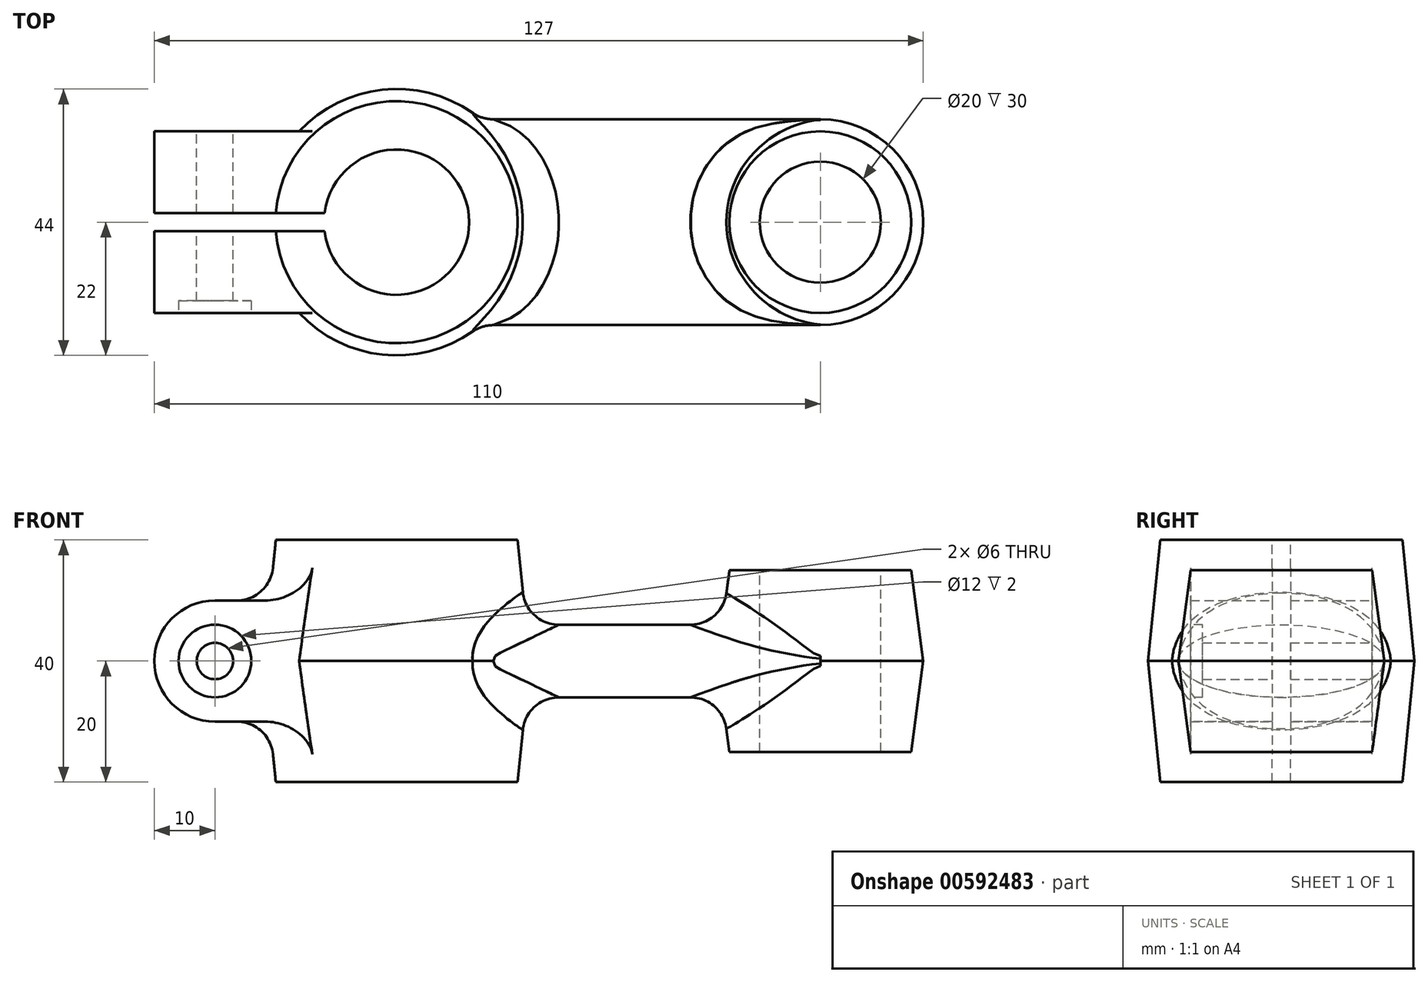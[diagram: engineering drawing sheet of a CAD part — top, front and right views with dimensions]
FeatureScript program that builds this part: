
annotation { "Feature Type Name" : "Feature", "Feature Type Description" : "" }
export const myFeature = defineFeature(function(context is Context, id is Id, definition is map)
    precondition{}
    {
        {
            var Q0;
            Q0=qCreatedBy(makeId("Front.planeOp"),FACE);
            var sketch = newSketch(context, id + "F0", { "sketchPlane" : qUnion([Q0])});
            skLineSegment(sketch, "E0", {"start": v(0, 0) * mm, "end": v(0, 67.9) * mm, "construction": true});
            skLineSegment(sketch, "E1", {"start": v(-22, 0) * mm, "end": v(-20, 20) * mm});
            skLineSegment(sketch, "E2", {"start": v(-20, 20) * mm, "end": v(0, 20) * mm});
            skLineSegment(sketch, "E3", {"start": v(0, 20) * mm, "end": v(0, -20) * mm});
            skLineSegment(sketch, "E4", {"start": v(0, -20) * mm, "end": v(-20, -20) * mm});
            skLineSegment(sketch, "E5", {"start": v(-20, -20) * mm, "end": v(-22, 0) * mm});
            skLineSegment(sketch, "E6", {"start": v(0, 0) * mm, "end": v(-22, 0) * mm, "construction": true});
            skLineSegment(sketch, "E7", {"start": v(-20, 20) * mm, "end": v(-20, -20) * mm, "construction": true});
            skSolve(sketch);
        }
        {
            var Q0;
            Q0=makeQuery(id+"F0.imprint","IMPRINT",FACE,{"disambiguationData":[TD([[makeQuery(id+"F0.imprint","IMPRINT",EDGE,{"derivedFrom":sQuery(id+"F0.wireOp",EDGE,"E1")}),-1.0]])]});
            var Q1;
            Q1=sQuery(id+"F0.wireOp",EDGE,"E0");
            revolve(context, id + "F1", {"entities" : qUnion([Q0]), "axis" : qUnion([Q1]), "revolveType" : RevolveType.FULL});
        }
        {
            var Q0;
            Q0=qCreatedBy(makeId("Right.planeOp"),FACE);
            var sketch = newSketch(context, id + "F2", { "sketchPlane" : qUnion([Q0])});
            skLineSegment(sketch, "E8", {"start": v(0, 0) * mm, "end": v(17, 0) * mm, "construction": true});
            skLineSegment(sketch, "E9", {"start": v(0, 0) * mm, "end": v(0, 6) * mm, "construction": true});
            skEllipse(sketch, "E10", {"center": v(0, 0) * mm, "majorRadius": 6 * mm, "minorRadius": 17 * mm, "majorAxis": v(0, 1)});
            skSolve(sketch);
        }
        {
            var Q0;
            Q0 = qSketchRegion(id + "F2", true);
            extrude(context, id + "F3", {"entities" : qUnion([Q0]), "operationType" : NewBodyOperationType.ADD, "depth" : 70 * mm, "offsetDistance" : 25 * mm});
        }
        {
            var Q0;
            Q0=qCreatedBy(makeId("Front.planeOp"),FACE);
            var sketch = newSketch(context, id + "F4", { "sketchPlane" : qUnion([Q0])});
            skLineSegment(sketch, "E11.0", {"start": v(70, 6) * mm, "end": v(70, -6) * mm, "construction": true});
            skLineSegment(sketch, "E12", {"start": v(70, -15) * mm, "end": v(70, 15) * mm});
            skLineSegment(sketch, "E13", {"start": v(70, 15) * mm, "end": v(85, 15) * mm});
            skLineSegment(sketch, "E14", {"start": v(85, 15) * mm, "end": v(87, 0) * mm});
            skLineSegment(sketch, "E15", {"start": v(87, 0) * mm, "end": v(85, -15) * mm});
            skLineSegment(sketch, "E16", {"start": v(85, -15) * mm, "end": v(70, -15) * mm});
            skLineSegment(sketch, "E17", {"start": v(0, 0) * mm, "end": v(87, 0) * mm, "construction": true});
            skSolve(sketch);
        }
        {
            var Q0;
            Q0=makeQuery(id+"F4.imprint","IMPRINT",FACE,{"disambiguationData":[TD([[makeQuery(id+"F4.imprint","IMPRINT",EDGE,{"derivedFrom":sQuery(id+"F4.wireOp",EDGE,"E12")}),-1.0]])]});
            var Q1;
            Q1=sQuery(id+"F4.wireOp",EDGE,"E12");
            revolve(context, id + "F5", {"operationType" : NewBodyOperationType.ADD, "entities" : qUnion([Q0]), "axis" : qUnion([Q1]), "revolveType" : RevolveType.FULL});
        }
        {
            var Q0;
            Q0=qCreatedBy(makeId("Front.planeOp"),FACE);
            var sketch = newSketch(context, id + "F6", { "sketchPlane" : qUnion([Q0])});
            skLineSegment(sketch, "E18", {"start": v(0, -10) * mm, "end": v(0, 10) * mm});
            skLineSegment(sketch, "E19", {"start": v(0, 10) * mm, "end": v(-30, 10) * mm});
            skLineSegment(sketch, "E20", {"start": v(-30, 10) * mm, "end": v(-30, -10) * mm, "construction": true});
            skLineSegment(sketch, "E21", {"start": v(-30, -10) * mm, "end": v(0, -10) * mm});
            skArc(sketch, "E22", {"start": v(-30, 10) * mm, "mid": v(-40, 0) * mm, "end": v(-30, -10) * mm});
            skCircle(sketch, "E23", {"center": v(-30, 0) * mm, "radius": 3 * mm});
            skPoint(sketch, "E24", {"position": v(-40, 0) * mm});
            skPoint(sketch, "E25", {"position": v(0, 0) * mm});
            skSolve(sketch);
        }
        {
            var Q0;
            Q0=makeQuery(id+"F6.imprint","IMPRINT",FACE,{"disambiguationData":[TD([[makeQuery(id+"F6.imprint","IMPRINT",EDGE,{"derivedFrom":sQuery(id+"F6.wireOp",EDGE,"E18")}),1.0]])]});
            extrude(context, id + "F7", {"entities" : qUnion([Q0]), "operationType" : NewBodyOperationType.ADD, "endBound" : BoundingType.SYMMETRIC, "depth" : 30 * mm, "offsetDistance" : 25 * mm});
        }
        {
            var Q0;
            Q0=makeQuery(id+"F7.opExtrude","CAP_FACE",FACE,{"disambiguationData":[OSD([sQuery(id+"F6.wireOp",EDGE,"E18"),sQuery(id+"F6.wireOp",EDGE,"E19"),sQuery(id+"F6.wireOp",EDGE,"E21"),sQuery(id+"F6.wireOp",EDGE,"E22"),sQuery(id+"F6.wireOp",EDGE,"E23")])],"isStart":false});
            var sketch = newSketch(context, id + "F8", { "sketchPlane" : qUnion([Q0])});
            skCircle(sketch, "E26", {"center": v(-30, 0) * mm, "radius": 6 * mm});
            skSolve(sketch);
        }
        {
            var Q0;
            Q0 = qSketchRegion(id + "F8", true);
            extrude(context, id + "F9", {"entities" : qUnion([Q0]), "operationType" : NewBodyOperationType.REMOVE, "oppositeDirection" : true, "depth" : 2 * mm, "offsetDistance" : 25 * mm});
        }
        {
            var Q0;
            Q0=makeQuery(id+"F3.boolean.opBoolean","INTERSECT",EDGE,{"derivedFrom":[makeQuery(id+"F1.opRevolve","SWEPT_FACE",FACE,{"disambiguationData":[OSD([sQuery(id+"F0.wireOp",EDGE,"E1")])]}),makeQuery(id+"F3.opExtrude","SWEPT_FACE",FACE,{"disambiguationData":[OSD([sQuery(id+"F2.wireOp",EDGE,"E10")])]})]});
            var Q1;
            Q1=makeQuery(id+"F3.boolean.opBoolean","INTERSECT",EDGE,{"derivedFrom":[makeQuery(id+"F1.opRevolve","SWEPT_FACE",FACE,{"disambiguationData":[OSD([sQuery(id+"F0.wireOp",EDGE,"E5")])]}),makeQuery(id+"F3.opExtrude","SWEPT_FACE",FACE,{"disambiguationData":[OSD([sQuery(id+"F2.wireOp",EDGE,"E10")])]})]});
            fillet(context, id + "F10", {"entities" : qUnion([Q0, Q1]), "radius" : 6 * mm, "tangentPropagation" : true, "allowEdgeOverflow" : false});
        }
        {
            var Q0;
            Q0=makeQuery(id+"F5.boolean.opBoolean","INTERSECT",EDGE,{"derivedFrom":[makeQuery(id+"F3.opExtrude","SWEPT_FACE",FACE,{"disambiguationData":[OSD([sQuery(id+"F2.wireOp",EDGE,"E10")])]}),makeQuery(id+"F5.opRevolve","SWEPT_FACE",FACE,{"disambiguationData":[OSD([sQuery(id+"F4.wireOp",EDGE,"E14")])]})]});
            var Q1;
            Q1=makeQuery(id+"F5.boolean.opBoolean","INTERSECT",EDGE,{"derivedFrom":[makeQuery(id+"F3.opExtrude","SWEPT_FACE",FACE,{"disambiguationData":[OSD([sQuery(id+"F2.wireOp",EDGE,"E10")])]}),makeQuery(id+"F5.opRevolve","SWEPT_FACE",FACE,{"disambiguationData":[OSD([sQuery(id+"F4.wireOp",EDGE,"E15")])]})]});
            fillet(context, id + "F11", {"entities" : qUnion([Q0, Q1]), "radius" : 6 * mm, "tangentPropagation" : true, "allowEdgeOverflow" : false});
        }
        {
            var Q0;
            Q0=makeQuery(id+"F7.boolean.opBoolean","INTERSECT",EDGE,{"derivedFrom":[makeQuery(id+"F1.opRevolve","SWEPT_FACE",FACE,{"disambiguationData":[OSD([sQuery(id+"F0.wireOp",EDGE,"E1")])]}),makeQuery(id+"F7.opExtrude","SWEPT_FACE",FACE,{"disambiguationData":[OSD([sQuery(id+"F6.wireOp",EDGE,"E19")])]})]});
            var Q1;
            Q1=makeQuery(id+"F7.boolean.opBoolean","INTERSECT",EDGE,{"derivedFrom":[makeQuery(id+"F1.opRevolve","SWEPT_FACE",FACE,{"disambiguationData":[OSD([sQuery(id+"F0.wireOp",EDGE,"E5")])]}),makeQuery(id+"F7.opExtrude","SWEPT_FACE",FACE,{"disambiguationData":[OSD([sQuery(id+"F6.wireOp",EDGE,"E21")])]})]});
            fillet(context, id + "F12", {"entities" : qUnion([Q0, Q1]), "radius" : 6 * mm, "tangentPropagation" : true, "allowEdgeOverflow" : false});
        }
        {
            var Q0;
            Q0=qCreatedBy(makeId("Top.planeOp"),FACE);
            var sketch = newSketch(context, id + "F13", { "sketchPlane" : qUnion([Q0])});
            skArc(sketch, "E27", {"start": v(-11.9, -1.5) * mm, "mid": v(12, 0) * mm, "end": v(-11.9, 1.5) * mm});
            skCircle(sketch, "E28", {"center": v(70, 0) * mm, "radius": 10 * mm});
            skLineSegment(sketch, "E29.bottom", {"start": v(-83.06, 1.5) * mm, "end": v(-11.9, 1.5) * mm});
            skLineSegment(sketch, "E29.top", {"start": v(-83.06, -1.5) * mm, "end": v(-11.9, -1.5) * mm});
            skLineSegment(sketch, "E29.left", {"start": v(-83.06, 1.5) * mm, "end": v(-83.06, -1.5) * mm});
            skPoint(sketch, "E30", {"position": v(-83.06, 0) * mm});
            skPoint(sketch, "E31.orphan", {"position": v(0, 1.5) * mm});
            skSolve(sketch);
        }
        {
            var Q0;
            Q0 = qSketchRegion(id + "F13", true);
            extrude(context, id + "F14", {"entities" : qUnion([Q0]), "operationType" : NewBodyOperationType.REMOVE, "endBound" : BoundingType.SYMMETRIC, "oppositeDirection" : true, "depth" : 100 * mm, "offsetDistance" : 25 * mm});
        }
    });
